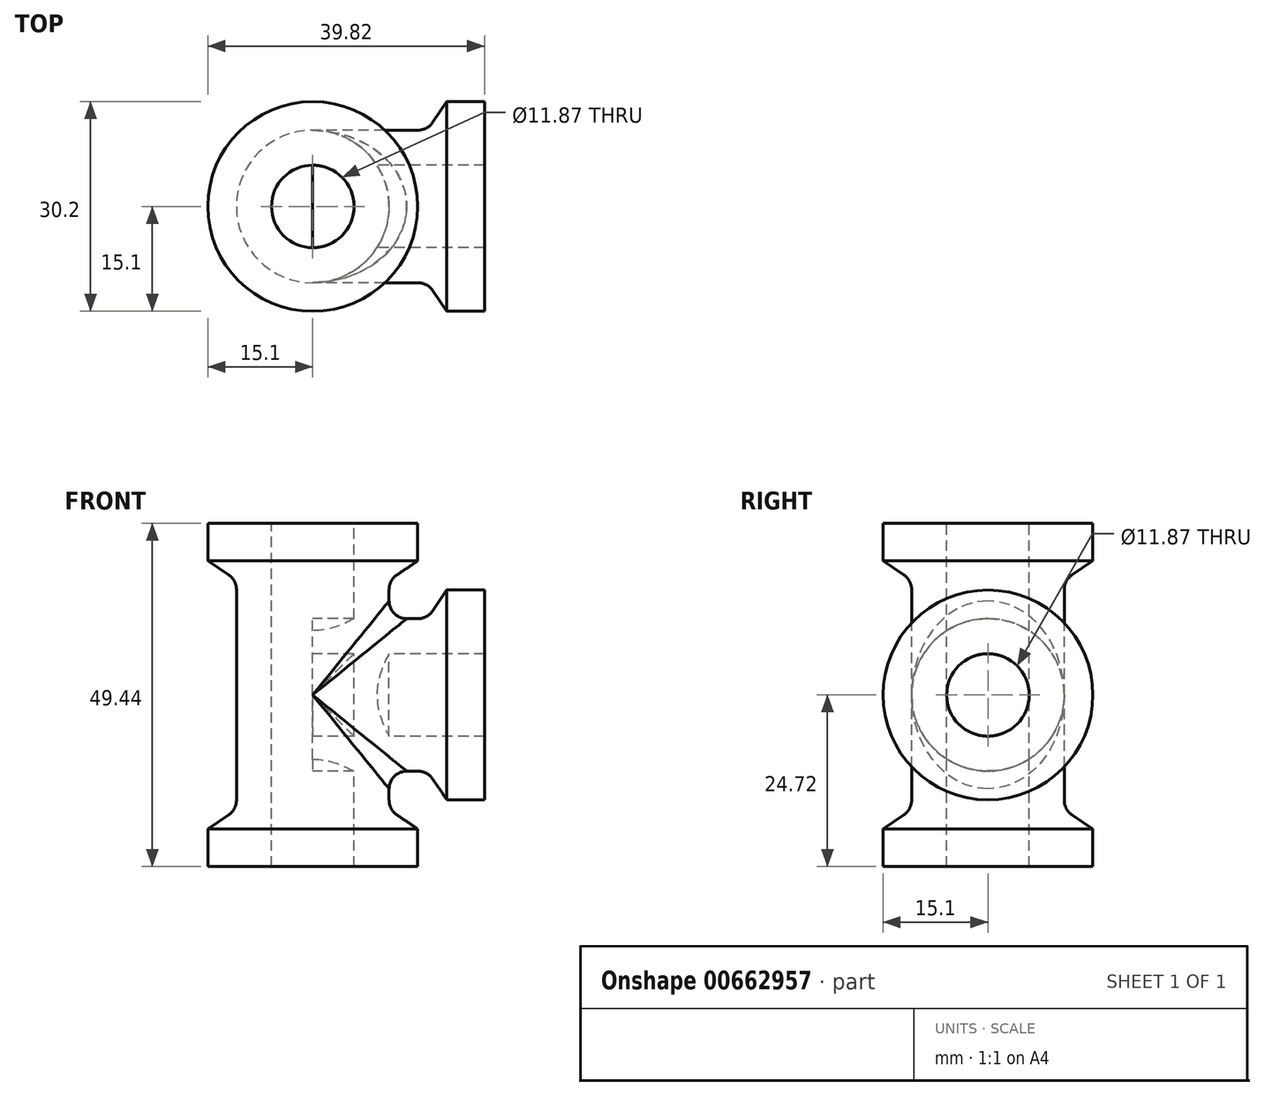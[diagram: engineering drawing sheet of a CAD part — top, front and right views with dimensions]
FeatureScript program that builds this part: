
annotation { "Feature Type Name" : "Feature", "Feature Type Description" : "" }
export const myFeature = defineFeature(function(context is Context, id is Id, definition is map)
    precondition{}
    {
        {
            var Q0;
            Q0=qCreatedBy(makeId("Front.planeOp"),FACE);
            var sketch = newSketch(context, id + "F0", { "sketchPlane" : qUnion([Q0])});
            skLineSegment(sketch, "E0", {"start": v(-5.94, 24.72) * mm, "end": v(-15.1, 24.72) * mm});
            skLineSegment(sketch, "E1", {"start": v(-15.1, 24.72) * mm, "end": v(-15.1, 19.3) * mm});
            skLineSegment(sketch, "E2", {"start": v(-15.1, 19.3) * mm, "end": v(-10.98, 16.5) * mm});
            skLineSegment(sketch, "E3", {"start": v(-10.98, 16.5) * mm, "end": v(-10.98, 0) * mm});
            skLineSegment(sketch, "E4", {"start": v(-5.94, 24.72) * mm, "end": v(-5.94, 0) * mm});
            skLineSegment(sketch, "E5", {"start": v(-5.94, 0) * mm, "end": v(-10.98, 0) * mm});
            skLineSegment(sketch, "E6", {"start": v(0, 48.65) * mm, "end": v(0, 12.01) * mm, "construction": true});
            skLineSegment(sketch, "E7", {"start": v(-33.08, -33.08) * mm, "end": v(37.96, 37.96) * mm, "construction": true});
            skLineSegment(sketch, "E8.MirrorCS", {"start": v(-5.94, -24.72) * mm, "end": v(-5.94, 0) * mm});
            skLineSegment(sketch, "E9.MirrorCS", {"start": v(-10.98, -16.5) * mm, "end": v(-10.98, 0) * mm});
            skLineSegment(sketch, "E10.MirrorCS", {"start": v(-15.1, -19.3) * mm, "end": v(-10.98, -16.5) * mm});
            skLineSegment(sketch, "E11.MirrorCS", {"start": v(-5.94, -24.72) * mm, "end": v(-15.1, -24.72) * mm});
            skLineSegment(sketch, "E12.MirrorCS", {"start": v(-15.1, -24.72) * mm, "end": v(-15.1, -19.3) * mm});
            skLineSegment(sketch, "E13.MirrorCS", {"start": v(16.5, -10.98) * mm, "end": v(0, -10.98) * mm});
            skLineSegment(sketch, "E14.MirrorCS", {"start": v(19.3, -15.1) * mm, "end": v(16.5, -10.98) * mm});
            skLineSegment(sketch, "E15.MirrorCS", {"start": v(24.72, -5.94) * mm, "end": v(0, -5.94) * mm});
            skLineSegment(sketch, "E16.MirrorCS", {"start": v(24.72, -5.94) * mm, "end": v(24.72, -15.1) * mm});
            skLineSegment(sketch, "E17.MirrorCS", {"start": v(24.72, -15.1) * mm, "end": v(19.3, -15.1) * mm});
            skLineSegment(sketch, "E18.MirrorCS", {"start": v(0, -5.94) * mm, "end": v(0, -10.98) * mm});
            skLineSegment(sketch, "E19", {"start": v(10.33, 0) * mm, "end": v(33.5, 0) * mm, "construction": true});
            skSolve(sketch);
        }
        {
            var Q0;
            Q0=makeQuery(id+"F0.imprint","IMPRINT",FACE,{"disambiguationData":[TD([[makeQuery(id+"F0.imprint","IMPRINT",EDGE,{"derivedFrom":sQuery(id+"F0.wireOp",EDGE,"E0")}),1.0]])]});
            var Q1;
            Q1=makeQuery(id+"F0.imprint","IMPRINT",FACE,{"disambiguationData":[TD([[makeQuery(id+"F0.imprint","IMPRINT",EDGE,{"derivedFrom":sQuery(id+"F0.wireOp",EDGE,"E5")}),1.0]])]});
            var Q2;
            Q2=sQuery(id+"F0.wireOp",EDGE,"E11.MirrorCS");
            var Q3;
            Q3=sQuery(id+"F0.wireOp",EDGE,"E1");
            var Q4;
            Q4=sQuery(id+"F0.wireOp",EDGE,"E10.MirrorCS");
            var Q5;
            Q5=sQuery(id+"F0.wireOp",EDGE,"E2");
            var Q6;
            Q6=sQuery(id+"F0.wireOp",EDGE,"E0");
            var Q7;
            Q7=sQuery(id+"F0.wireOp",EDGE,"E8.MirrorCS");
            var Q8;
            Q8=sQuery(id+"F0.wireOp",EDGE,"E12.MirrorCS");
            var Q9;
            Q9=sQuery(id+"F0.wireOp",EDGE,"E3");
            var Q10;
            Q10=sQuery(id+"F0.wireOp",EDGE,"E4");
            var Q11;
            Q11=sQuery(id+"F0.wireOp",EDGE,"E9.MirrorCS");
            var Q12;
            Q12=sQuery(id+"F0.wireOp",EDGE,"E5");
            var Q13;
            Q13=sQuery(id+"F0.wireOp",EDGE,"E6");
            revolve(context, id + "F1", {"entities" : qUnion([Q0, Q1]), "surfaceEntities" : qUnion([Q2, Q3, Q4, Q5, Q6, Q7, Q8, Q9, Q10, Q11, Q12]), "axis" : qUnion([Q13]), "revolveType" : RevolveType.FULL});
        }
        {
            var Q0;
            Q0=makeQuery(id+"F0.imprint","IMPRINT",FACE,{"disambiguationData":[TD([[makeQuery(id+"F0.imprint","IMPRINT",EDGE,{"derivedFrom":sQuery(id+"F0.wireOp",EDGE,"E13.MirrorCS")}),-1.0]])]});
            var Q1;
            Q1=sQuery(id+"F0.wireOp",EDGE,"E19");
            revolve(context, id + "F2", {"operationType" : NewBodyOperationType.ADD, "entities" : qUnion([Q0]), "axis" : qUnion([Q1]), "revolveType" : RevolveType.FULL});
        }
        {
            var Q0;
            Q0=makeQuery(id+"F1.opRevolve","SWEPT_EDGE",EDGE,{"disambiguationData":[OSD([sQuery(id+"F0.wireOp",EDGE,"E2"),sQuery(id+"F0.wireOp",EDGE,"E3")])]});
            var Q1;
            Q1=makeQuery(id+"F2.boolean.opBoolean","INTERSECT",EDGE,{"disambiguationData":[OD(1.0)],"derivedFrom":[makeQuery(id+"F1.opRevolve","SWEPT_FACE",FACE,{"disambiguationData":[OSD([sQuery(id+"F0.wireOp",EDGE,"E3"),sQuery(id+"F0.wireOp",EDGE,"E9.MirrorCS")])]}),makeQuery(id+"F2.opRevolve","SWEPT_FACE",FACE,{"disambiguationData":[OSD([sQuery(id+"F0.wireOp",EDGE,"E13.MirrorCS")])]})]});
            var Q2;
            Q2=makeQuery(id+"F2.opRevolve","SWEPT_EDGE",EDGE,{"disambiguationData":[OSD([sQuery(id+"F0.wireOp",EDGE,"E13.MirrorCS"),sQuery(id+"F0.wireOp",EDGE,"E14.MirrorCS")])]});
            var Q3;
            Q3=makeQuery(id+"F2.boolean.opBoolean","INTERSECT",EDGE,{"disambiguationData":[OD(0.0)],"derivedFrom":[makeQuery(id+"F1.opRevolve","SWEPT_FACE",FACE,{"disambiguationData":[OSD([sQuery(id+"F0.wireOp",EDGE,"E3"),sQuery(id+"F0.wireOp",EDGE,"E9.MirrorCS")])]}),makeQuery(id+"F2.opRevolve","SWEPT_FACE",FACE,{"disambiguationData":[OSD([sQuery(id+"F0.wireOp",EDGE,"E13.MirrorCS")])]})]});
            var Q4;
            Q4=makeQuery(id+"F1.opRevolve","SWEPT_EDGE",EDGE,{"disambiguationData":[OSD([sQuery(id+"F0.wireOp",EDGE,"E9.MirrorCS"),sQuery(id+"F0.wireOp",EDGE,"E10.MirrorCS")])]});
            fillet(context, id + "F3", {"entities" : qUnion([Q0, Q1, Q2, Q3, Q4]), "radius" : 2.54 * mm, "tangentPropagation" : true, "allowEdgeOverflow" : false});
        }
    });
